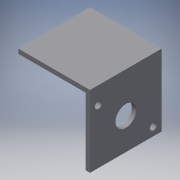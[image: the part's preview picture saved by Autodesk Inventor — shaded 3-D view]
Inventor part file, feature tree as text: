
AUTODESK INVENTOR PART (.ipt)
format: ipt  version: 2016 (Build 200138000, 138)  size: 111,616 bytes
history: native  units: in
note: dims shown in document units (in); Inventor stores cm internally (conversion verified against a paired STEP export)
features: extrude x2, sketch x2
ambient origin geometry x8: Origin, YZ Plane, XZ Plane, XY Plane, X Axis, Y Axis, Z Axis, Center Point
bodies: Solid1 (feature_tree)
feature tree (4):
  extrude  "Extrusion1"  Depth=0.125in
  extrude  "Extrusion2"  Depth=1.875in
  sketch  "Sketch1"  dims[d0=2.0in d1=0.125in]
  sketch  "Sketch2"  dims[d2=1.875in d3=1.875in d4=2.0in d5=0.0in d9=1.0in d10=0.875in d11=0.125in d12=0.0in d13=2.0in d14=0.1875in d15=0.1875in d16=0.233in d17=0.75in]
